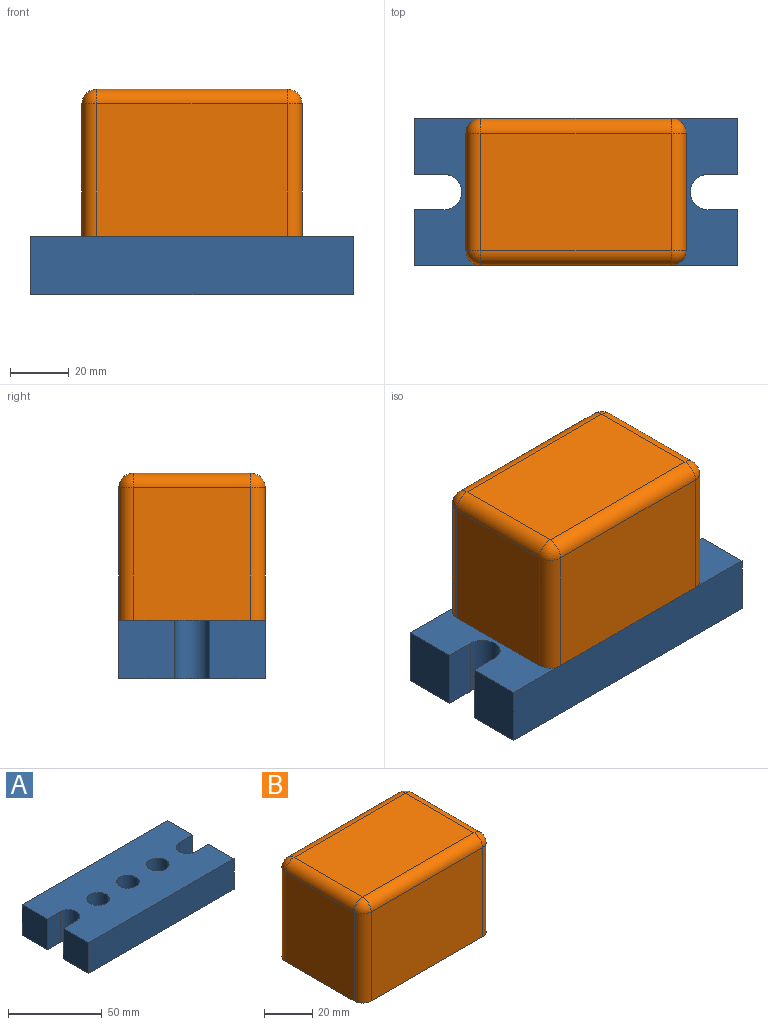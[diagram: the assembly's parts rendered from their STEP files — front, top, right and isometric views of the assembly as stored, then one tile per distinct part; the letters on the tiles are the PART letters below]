
ASSEMBLY  parts=2 mates=1
PART A: 23 faces, bbox 110x50x20 mm
  f0: plane 20x10mm, normal (0,1,0), area 200mm2, adj f1,f11,f12,f13
  f1: plane 20x19mm, normal (-1,0,0), area 380mm2, adj f0,f2,f12,f13
  f2: plane 110x20mm, normal (0,-1,0), area 2200mm2, adj f1,f3,f12,f13
  f3: plane 20x19mm, normal (1,0,0), area 380mm2, adj f2,f4,f12,f13
  f4: plane 20x10mm, normal (0,1,0), area 200mm2, adj f3,f5,f12,f13
  f5: cylinder r=6mm len=20mm, axis (0,0,1), area 377mm2, adj f4,f6,f12,f13
  f6: plane 20x10mm, normal (0,-1,0), area 200mm2, adj f5,f7,f12,f13
  f7: plane 20x19mm, normal (1,0,0), area 380mm2, adj f6,f8,f12,f13
  f8: plane 110x20mm, normal (0,1,0), area 2200mm2, adj f7,f9,f12,f13
  f9: plane 20x19mm, normal (-1,0,0), area 380mm2, adj f8,f10,f12,f13
  f10: plane 20x10mm, normal (0,-1,0), area 200mm2, adj f9,f11,f12,f13
  f11: cylinder r=6mm len=20mm, axis (0,0,1), area 377mm2, adj f0,f10,f12,f13
  f12: plane 110x50mm, normal (0,0,-1), area 4911.3mm2, adj f0,f1,f2,f3,f4,f5,f6,f7
  f13: plane 110x50mm, normal (0,0,1), area 4807.6mm2, adj f0,f1,f2,f3,f4,f5,f6,f7
  f14: cylinder r=6mm len=15mm, axis (0,0,1), area 565.5mm2, adj f13,f15
  f15: plane 12x12mm, normal (0,0,1), area 34.6mm2, adj f14,f22
  f16: cylinder r=6mm len=15mm, axis (0,0,1), area 565.5mm2, adj f13,f17
  f17: plane 12x12mm, normal (0,0,1), area 34.6mm2, adj f16,f21
  f18: cylinder r=6mm len=15mm, axis (0,0,1), area 565.5mm2, adj f13,f19
  f19: plane 12x12mm, normal (0,0,1), area 34.6mm2, adj f18,f20
  f20: cylinder r=5mm len=10mm, axis (0,0,1), area 157.1mm2, adj f12,f19
  f21: cylinder r=5mm len=10mm, axis (0,0,1), area 157.1mm2, adj f12,f17
  f22: cylinder r=5mm len=10mm, axis (0,0,1), area 157.1mm2, adj f12,f15
PART B: 24 faces, bbox 75x50x50 mm
  f0: plane 65x45mm, normal (0,-1,0), area 2925mm2, adj f5,f8,f14,f17
  f1: plane 45x40mm, normal (1,0,0), area 1800mm2, adj f5,f11,f15,f17
  f2: plane 65x45mm, normal (0,1,0), area 2925mm2, adj f5,f6,f10,f11
  f3: plane 45x40mm, normal (-1,0,0), area 1800mm2, adj f5,f6,f8,f9
  f4: plane 65x40mm, normal (0,0,1), area 2600mm2, adj f9,f10,f14,f15
  f5: plane 75x50mm, normal (0,0,-1), area 3492.9mm2, adj f0,f1,f2,f3,f6,f8,f11,f17
  f6: cylinder r=5mm len=45mm, axis (0,0,1), area 353.4mm2, adj f2,f3,f5,f7
  f7: sphere r=5mm, area 39.3mm2, adj f6,f9,f10
  f8: cylinder r=5mm len=45mm, axis (0,0,-1), area 353.4mm2, adj f0,f3,f5,f12
  f9: cylinder r=5mm len=40mm, axis (0,1,0), area 314.2mm2, adj f3,f4,f7,f12
  f10: cylinder r=5mm len=65mm, axis (1,0,0), area 510.5mm2, adj f2,f4,f7,f13
  f11: cylinder r=5mm len=45mm, axis (0,0,-1), area 353.4mm2, adj f1,f2,f5,f13
  f12: sphere r=5mm, area 39.3mm2, adj f8,f9,f14
  f13: sphere r=5mm, area 39.3mm2, adj f10,f11,f15
  f14: cylinder r=5mm len=65mm, axis (-1,0,0), area 510.5mm2, adj f0,f4,f12,f16
  f15: cylinder r=5mm len=40mm, axis (0,-1,0), area 314.2mm2, adj f1,f4,f13,f16
  f16: sphere r=5mm, area 39.3mm2, adj f14,f15,f17
  f17: cylinder r=5mm len=45mm, axis (0,0,1), area 353.4mm2, adj f0,f1,f5,f16
  f18: cylinder r=5mm len=25mm, axis (0,0,-1), area 785.4mm2, adj f5,f19
  f19: plane 10x10mm, normal (0,0,-1), area 78.5mm2, adj f18
  f20: cylinder r=5mm len=25mm, axis (0,0,-1), area 785.4mm2, adj f5,f21
  f21: plane 10x10mm, normal (0,0,-1), area 78.5mm2, adj f20
  f22: cylinder r=5mm len=25mm, axis (0,0,-1), area 785.4mm2, adj f5,f23
  f23: plane 10x10mm, normal (0,0,-1), area 78.5mm2, adj f22
PLACE A at identity
PLACE B at identity
MATE fastened B.f20 <-> A.f16  axis (0,0,-1) through (0,0,0)mm
